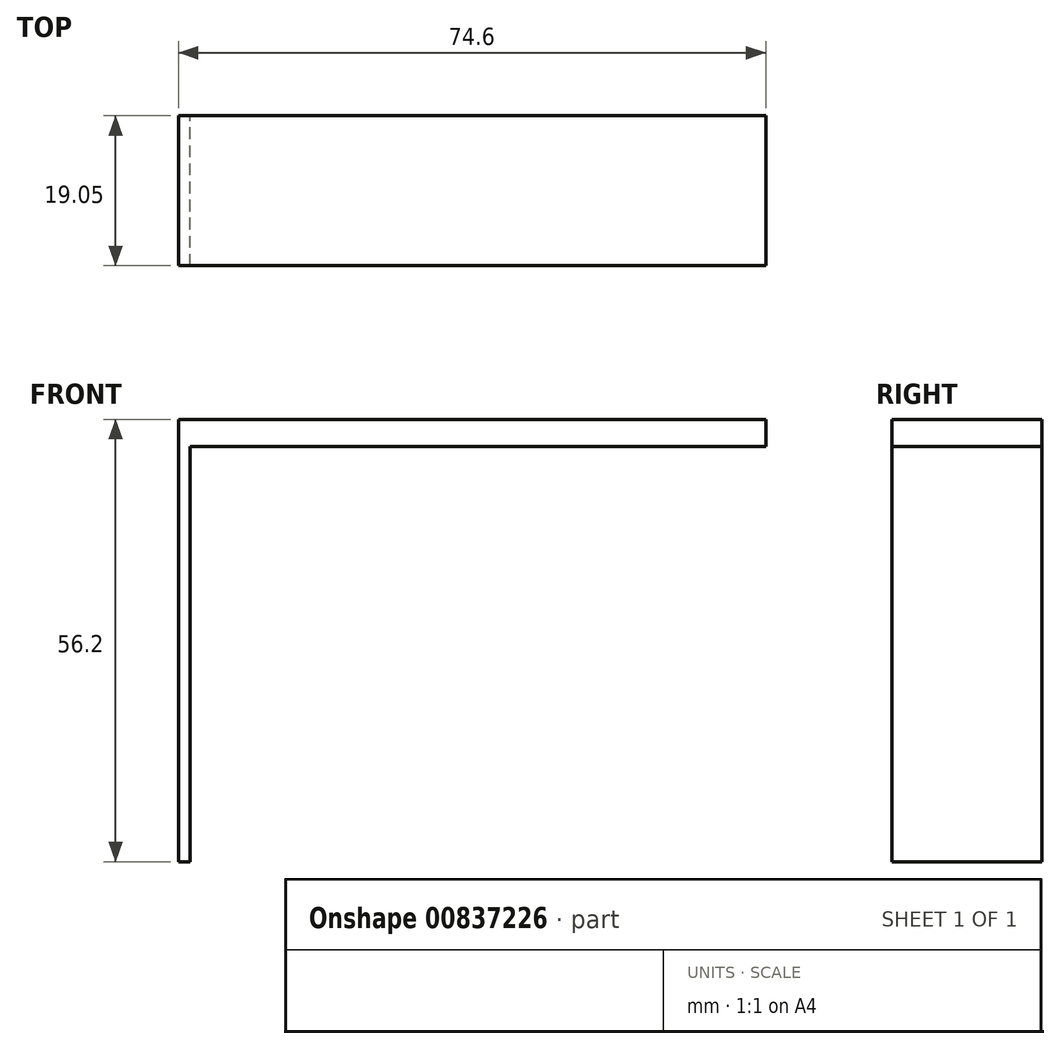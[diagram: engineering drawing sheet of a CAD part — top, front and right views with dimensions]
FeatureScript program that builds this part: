
annotation { "Feature Type Name" : "Feature", "Feature Type Description" : "" }
export const myFeature = defineFeature(function(context is Context, id is Id, definition is map)
    precondition{}
    {
        {
            var Q0;
            Q0=qCreatedBy(makeId("Front.planeOp"),FACE);
            var sketch = newSketch(context, id + "F0", { "sketchPlane" : qUnion([Q0])});
            skLineSegment(sketch, "E0.bottom", {"start": v(-38.7, 0) * mm, "end": v(-37.22, 0) * mm});
            skLineSegment(sketch, "E0.top", {"start": v(-38.7, -56.2) * mm, "end": v(-37.22, -56.2) * mm});
            skLineSegment(sketch, "E0.left", {"start": v(-38.7, 0) * mm, "end": v(-38.7, -56.2) * mm});
            skLineSegment(sketch, "E0.right", {"start": v(-37.22, 0) * mm, "end": v(-37.22, -56.2) * mm});
            skLineSegment(sketch, "E1.bottom", {"start": v(35.91, 0) * mm, "end": v(-37.22, 0) * mm});
            skLineSegment(sketch, "E1.top", {"start": v(35.91, -3.45) * mm, "end": v(-37.22, -3.45) * mm});
            skLineSegment(sketch, "E1.left", {"start": v(35.91, 0) * mm, "end": v(35.91, -3.45) * mm});
            skLineSegment(sketch, "E1.right", {"start": v(-37.22, 0) * mm, "end": v(-37.22, -3.45) * mm});
            skSolve(sketch);
        }
        {
            var Q0;
            Q0=makeQuery(id+"F0.imprint","IMPRINT",FACE,{"disambiguationData":[TD([[makeQuery(id+"F0.imprint","IMPRINT",EDGE,{"derivedFrom":sQuery(id+"F0.wireOp",EDGE,"E1.bottom")}),1.0]])]});
            var Q1;
            Q1 = qSketchRegion(id + "F0", true);
            extrude(context, id + "F1", {"entities" : qUnion([Q0, Q1]), "depth" : 19.05 * mm, "offsetDistance" : 25.4 * mm});
        }
    });
